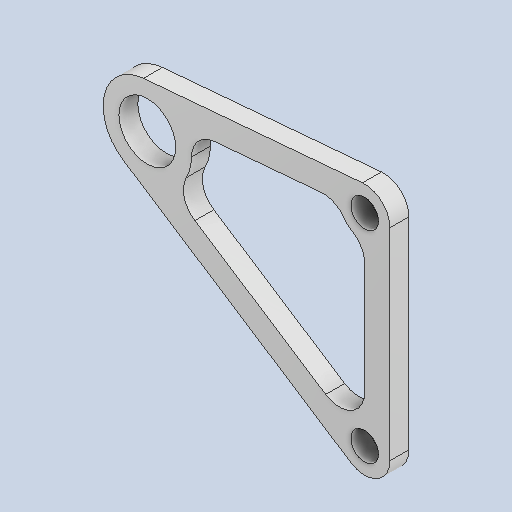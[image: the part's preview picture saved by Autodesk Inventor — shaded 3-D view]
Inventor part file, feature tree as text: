
AUTODESK INVENTOR PART (.ipt)
format: ipt  version: 2025.1 (Build 291241000, 241)  size: 210,944 bytes
history: native  units: mm
features: other x4, extrude x2, sketch x2, fillet x1, reference x1, projected_geometry x1
ambient origin geometry x8: Origin, YZ Plane, XZ Plane, XY Plane, X Axis, Y Axis, Z Axis, Center Point
bodies: Body1 (feature_tree)
feature tree (11):
  other  "ソリッド1"
  extrude  "押し出し1"  Depth=36.0mm
  extrude  "押し出し2"  Depth=16.0mm
  fillet  "フィレット1"  Radius=2.2mm
  sketch  "スケッチ1"
  other  "スケッチ矩形状パターン1"
  reference  "参照1"
  sketch  "スケッチ2"
  projected_geometry  "投影ループ1"
  other  "Assembly1"
  other  "02157_SmallDiameterHornB:4"
